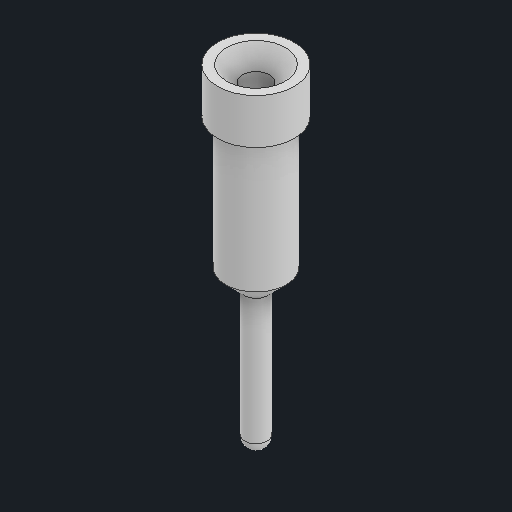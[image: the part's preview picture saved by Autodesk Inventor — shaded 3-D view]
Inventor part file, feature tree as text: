
AUTODESK INVENTOR PART (.ipt)
format: ipt  version: 2023 (Build 270158000, 158)  size: 91,648 bytes
history: native  units: in
note: dims shown in document units (in); Inventor stores cm internally (conversion verified against a paired STEP export)
features: revolve x1
ambient origin geometry x8: Origin, YZ Plane, XZ Plane, XY Plane, X Axis, Y Axis, Z Axis, Center Point
bodies: Solid1 (feature_tree)
feature tree (1):
  revolve  "Revolve1"  [1 undecoded]
note: 1 required parameter value undecoded (feature->parameter linkage not recoverable at this tier; creation-order binding heuristic only, values carry confidence <= 0.55)
